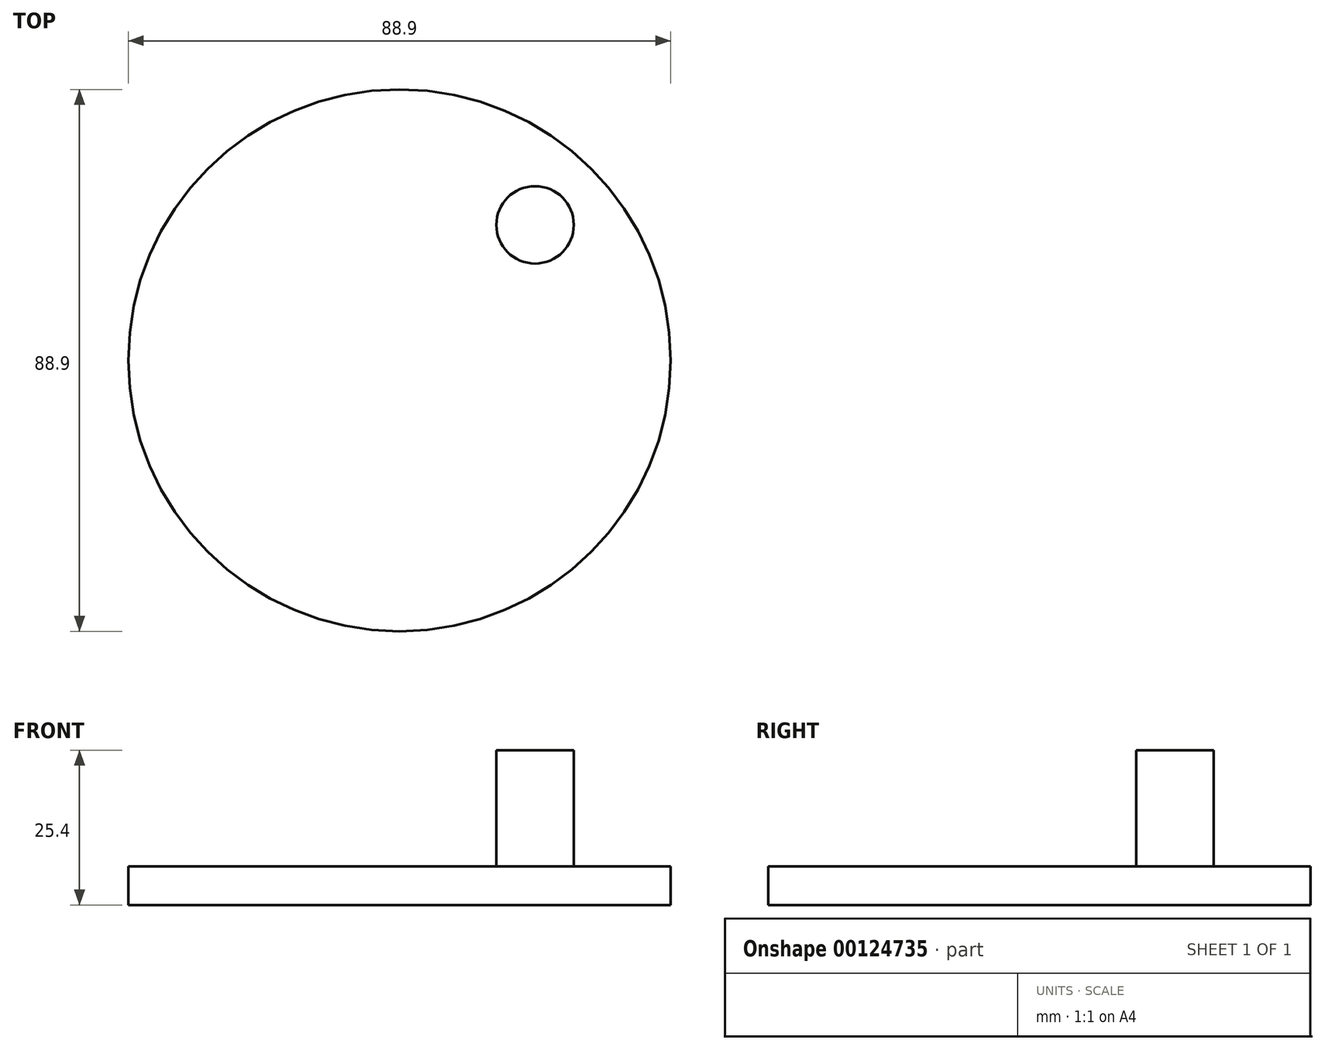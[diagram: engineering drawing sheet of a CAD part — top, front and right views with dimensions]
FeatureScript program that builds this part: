
annotation { "Feature Type Name" : "Feature", "Feature Type Description" : "" }
export const myFeature = defineFeature(function(context is Context, id is Id, definition is map)
    precondition{}
    {
        {
            var Q0;
            Q0=qCreatedBy(makeId("Top.planeOp"),FACE);
            var sketch = newSketch(context, id + "F0", { "sketchPlane" : qUnion([Q0])});
            skCircle(sketch, "E0", {"center": v(0, 0) * mm, "radius": 44.45 * mm});
            skSolve(sketch);
        }
        {
            var Q0;
            Q0=makeQuery(id+"F0.imprint","IMPRINT",FACE,{"disambiguationData":[TD([[makeQuery(id+"F0.imprint","IMPRINT",EDGE,{"derivedFrom":sQuery(id+"F0.wireOp",EDGE,"E0")}),1.0]])]});
            extrude(context, id + "F1", {"entities" : qUnion([Q0]), "depth" : 6.35 * mm});
        }
        {
            var Q0;
            Q0=makeQuery(id+"F1.opExtrude","CAP_FACE",FACE,{"disambiguationData":[OSD([sQuery(id+"F0.wireOp",EDGE,"E0")])],"isStart":false});
            var sketch = newSketch(context, id + "F2", { "sketchPlane" : qUnion([Q0])});
            skLineSegment(sketch, "E1", {"start": v(0, 44.45) * mm, "end": v(44.45, 0) * mm, "construction": true});
            skCircle(sketch, "E2", {"center": v(22.23, 22.23) * mm, "radius": 6.35 * mm});
            skSolve(sketch);
        }
        {
            var Q0;
            Q0 = qSketchRegion(id + "F2", true);
            extrude(context, id + "F3", {"entities" : qUnion([Q0]), "operationType" : NewBodyOperationType.ADD, "depth" : 19.05 * mm});
        }
    });
